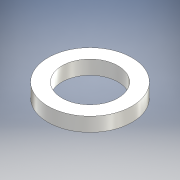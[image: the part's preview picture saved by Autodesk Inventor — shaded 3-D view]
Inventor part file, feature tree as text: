
AUTODESK INVENTOR PART (.ipt)
format: ipt  version: 2016 (Build 200138000, 138)  size: 98,816 bytes
history: native  units: mm
features: other x1, extrude x1, sketch x1
ambient origin geometry x8: Origin, YZ Plane, XZ Plane, XY Plane, X Axis, Y Axis, Z Axis, Center Point
bodies: Body1 (feature_tree)
feature tree (3):
  other  "ソリッド1"
  extrude  "押し出し1"  Depth=4.0mm
  sketch  "スケッチ1"
